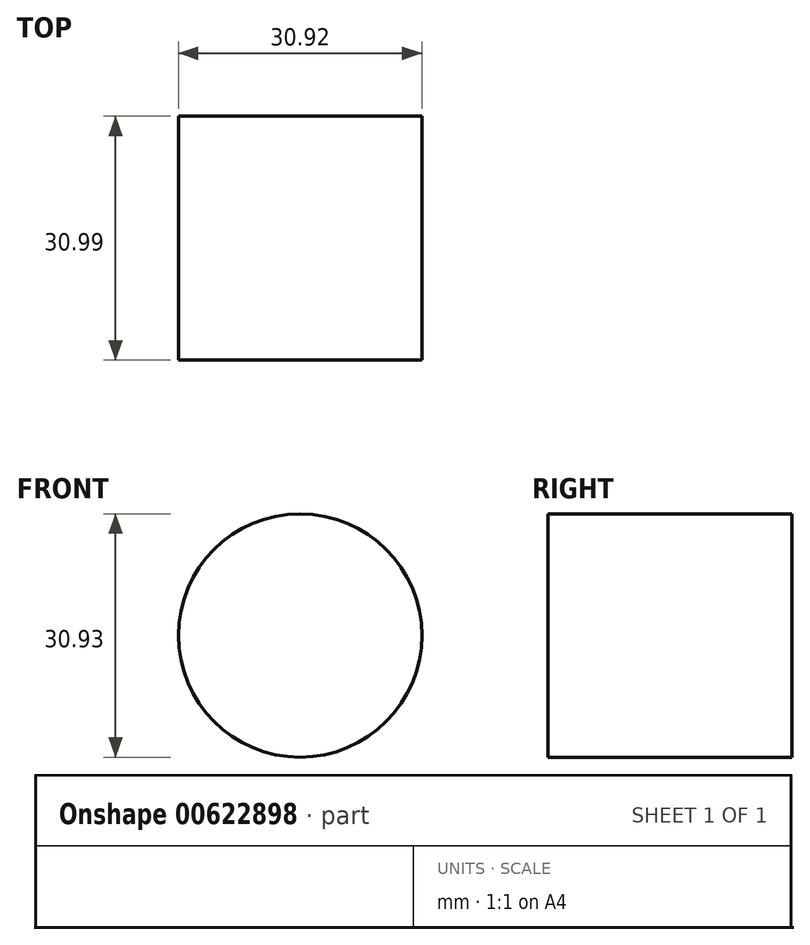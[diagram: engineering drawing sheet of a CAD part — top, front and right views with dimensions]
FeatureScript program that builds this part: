
annotation { "Feature Type Name" : "Feature", "Feature Type Description" : "" }
export const myFeature = defineFeature(function(context is Context, id is Id, definition is map)
    precondition{}
    {
        {
            var Q0;
            Q0=qCreatedBy(makeId("Front.planeOp"),FACE);
            var sketch = newSketch(context, id + "F0", { "sketchPlane" : qUnion([Q0])});
            skCircle(sketch, "E0", {"center": v(3.63, 4.22) * mm, "radius": 15.46 * mm});
            skSolve(sketch);
        }
        {
            var Q0;
            Q0 = qSketchRegion(id + "F0", true);
            extrude(context, id + "F1", {"entities" : qUnion([Q0]), "depth" : 30.99 * mm, "offsetDistance" : 25.4 * mm});
        }
    });
